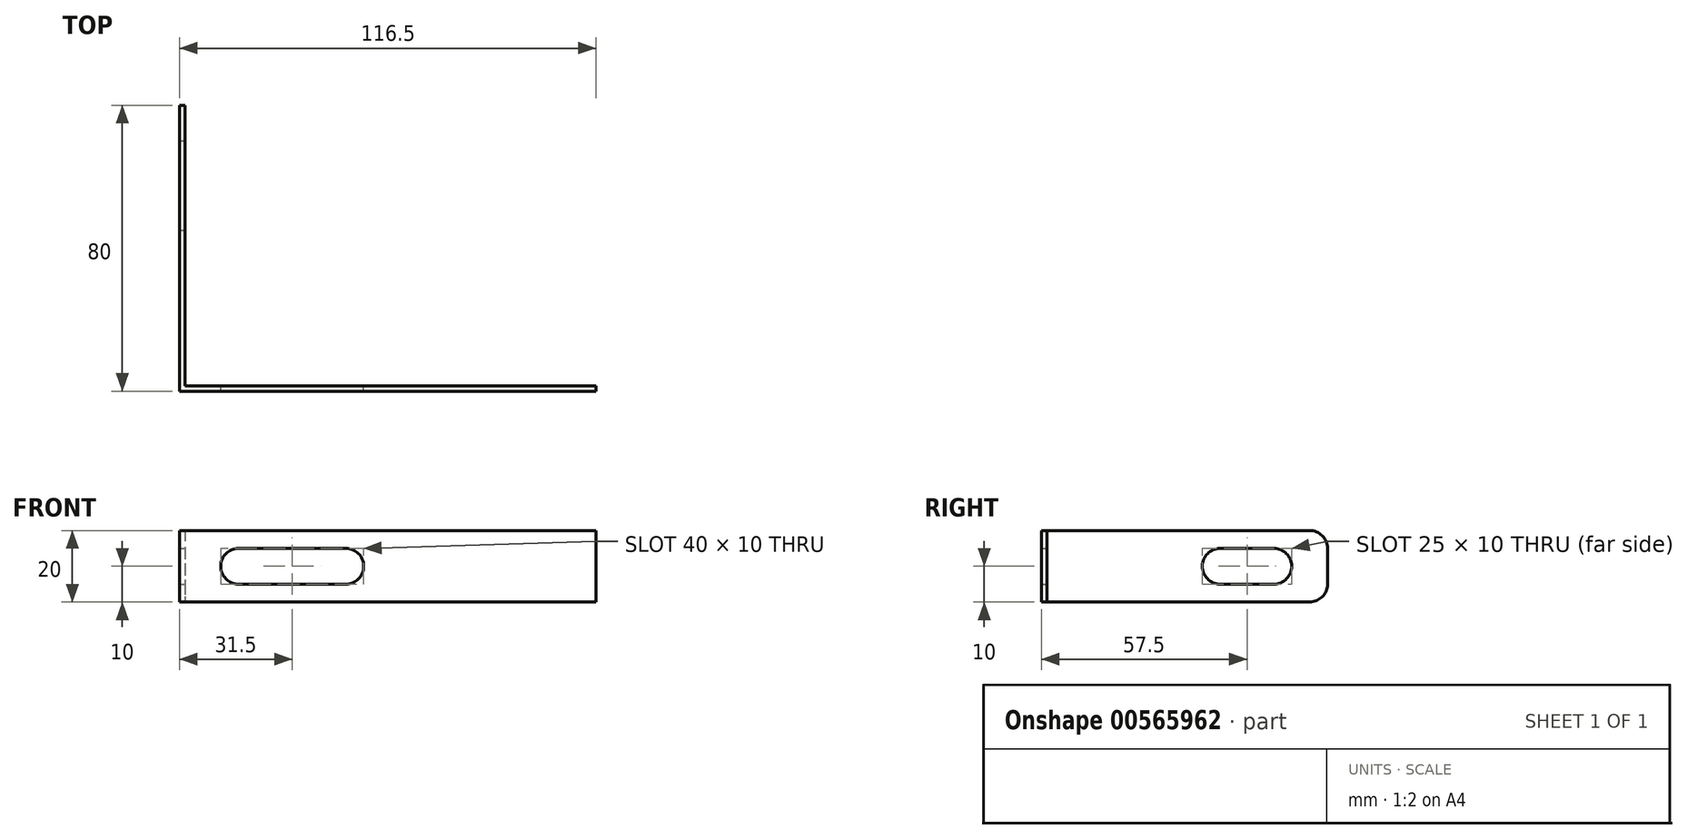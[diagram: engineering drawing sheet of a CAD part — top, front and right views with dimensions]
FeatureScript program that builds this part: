
annotation { "Feature Type Name" : "Feature", "Feature Type Description" : "" }
export const myFeature = defineFeature(function(context is Context, id is Id, definition is map)
    precondition{}
    {
        {
            var Q0;
            Q0=qCreatedBy(makeId("Front.planeOp"),FACE);
            var sketch = newSketch(context, id + "F0", { "sketchPlane" : qUnion([Q0])});
            skLineSegment(sketch, "E0", {"start": v(0, 10) * mm, "end": v(-115, 10) * mm});
            skLineSegment(sketch, "E1", {"start": v(-115, 10) * mm, "end": v(-115, -10) * mm});
            skLineSegment(sketch, "E2", {"start": v(-115, -10) * mm, "end": v(0, -10) * mm});
            skLineSegment(sketch, "E3.bottom", {"start": v(-70, -5) * mm, "end": v(-100, -5) * mm});
            skLineSegment(sketch, "E3.top", {"start": v(-70, 5) * mm, "end": v(-100, 5) * mm});
            skLineSegment(sketch, "E3.left", {"start": v(-65, 0) * mm, "end": v(-65, 0) * mm});
            skLineSegment(sketch, "E3.right", {"start": v(-105, 0) * mm, "end": v(-105, 0) * mm});
            skPoint(sketch, "E3.middle", {"position": v(-85, 0) * mm});
            skLineSegment(sketch, "E4.bottom", {"start": v(0, -5) * mm, "end": v(-50, -5) * mm});
            skLineSegment(sketch, "E4.top", {"start": v(0, 5) * mm, "end": v(-50, 5) * mm});
            skLineSegment(sketch, "E4.right", {"start": v(-55, 0) * mm, "end": v(-55, 0) * mm});
            skPoint(sketch, "E4.middle", {"position": v(-28.75, 0) * mm});
            skLineSegment(sketch, "E5", {"start": v(-60, 10) * mm, "end": v(-60, -10) * mm, "construction": true});
            skPoint(sketch, "E6.visualSharp", {"position": v(-105, 5) * mm});
            skArc(sketch, "E6.filletArc", {"start": v(-100, 5) * mm, "mid": v(-103.54, 3.54) * mm, "end": v(-105, 0) * mm});
            skPoint(sketch, "E7.visualSharp", {"position": v(-105, -5) * mm});
            skArc(sketch, "E7.filletArc", {"start": v(-105, 0) * mm, "mid": v(-103.54, -3.54) * mm, "end": v(-100, -5) * mm});
            skPoint(sketch, "E8.visualSharp", {"position": v(-65, -5) * mm});
            skArc(sketch, "E8.filletArc", {"start": v(-70, -5) * mm, "mid": v(-66.46, -3.54) * mm, "end": v(-65, 0) * mm});
            skPoint(sketch, "E9.visualSharp", {"position": v(-65, 5) * mm});
            skArc(sketch, "E9.filletArc", {"start": v(-65, 0) * mm, "mid": v(-66.46, 3.54) * mm, "end": v(-70, 5) * mm});
            skPoint(sketch, "E10.visualSharp", {"position": v(-55, 5) * mm});
            skArc(sketch, "E10.filletArc", {"start": v(-50, 5) * mm, "mid": v(-53.54, 3.54) * mm, "end": v(-55, 0) * mm});
            skPoint(sketch, "E11.visualSharp", {"position": v(-55, -5) * mm});
            skArc(sketch, "E11.filletArc", {"start": v(-55, 0) * mm, "mid": v(-53.54, -3.54) * mm, "end": v(-50, -5) * mm});
            skLineSegment(sketch, "E12", {"start": v(0, 10) * mm, "end": v(0, 0) * mm});
            skLineSegment(sketch, "E13", {"start": v(0, 0) * mm, "end": v(0, -10) * mm});
            skSolve(sketch);
        }
        {
            var Q0;
            Q0 = qSketchRegion(id + "F0", true);
            extrude(context, id + "F1", {"entities" : qUnion([Q0]), "depth" : 1.5 * mm, "offsetDistance" : 25 * mm});
        }
        {
            var Q0;
            Q0=makeQuery(id+"F1.opExtrude","SWEPT_FACE",FACE,{"disambiguationData":[OSD([sQuery(id+"F0.wireOp",EDGE,"E1")])]});
            var sketch = newSketch(context, id + "F2", { "sketchPlane" : qUnion([Q0])});
            skLineSegment(sketch, "E14.0", {"start": v(1.5, 10) * mm, "end": v(1.5, -10) * mm});
            skLineSegment(sketch, "E15", {"start": v(1.5, 10) * mm, "end": v(-73.5, 10) * mm});
            skLineSegment(sketch, "E16", {"start": v(-78.5, 5) * mm, "end": v(-78.5, -5) * mm});
            skLineSegment(sketch, "E17", {"start": v(-73.5, -10) * mm, "end": v(1.5, -10) * mm});
            skLineSegment(sketch, "E18", {"start": v(0, 0) * mm, "end": v(-78.5, 0) * mm, "construction": true});
            skPoint(sketch, "E18.endSnap0", {"position": v(-78.5, 0) * mm});
            skLineSegment(sketch, "E19.bottom", {"start": v(-63.5, -5) * mm, "end": v(-48.5, -5) * mm});
            skLineSegment(sketch, "E19.top", {"start": v(-63.5, 5) * mm, "end": v(-48.5, 5) * mm});
            skLineSegment(sketch, "E19.left", {"start": v(-68.5, 0) * mm, "end": v(-68.5, 0) * mm});
            skLineSegment(sketch, "E19.right", {"start": v(-43.5, 0) * mm, "end": v(-43.5, 0) * mm});
            skPoint(sketch, "E19.middle", {"position": v(-56, 0) * mm});
            skLineSegment(sketch, "E20", {"start": v(-34, 10) * mm, "end": v(-34, -10) * mm, "construction": true});
            skPoint(sketch, "E21.visualSharp", {"position": v(-68.5, 5) * mm});
            skArc(sketch, "E21.filletArc", {"start": v(-63.5, 5) * mm, "mid": v(-67.04, 3.54) * mm, "end": v(-68.5, 0) * mm});
            skPoint(sketch, "E22.visualSharp", {"position": v(-68.5, -5) * mm});
            skArc(sketch, "E22.filletArc", {"start": v(-68.5, 0) * mm, "mid": v(-67.04, -3.54) * mm, "end": v(-63.5, -5) * mm});
            skPoint(sketch, "E23.visualSharp", {"position": v(-43.5, -5) * mm});
            skArc(sketch, "E23.filletArc", {"start": v(-48.5, -5) * mm, "mid": v(-44.96, -3.54) * mm, "end": v(-43.5, 0) * mm});
            skPoint(sketch, "E24.visualSharp", {"position": v(-43.5, 5) * mm});
            skArc(sketch, "E24.filletArc", {"start": v(-43.5, 0) * mm, "mid": v(-44.96, 3.54) * mm, "end": v(-48.5, 5) * mm});
            skPoint(sketch, "E25.visualSharp", {"position": v(-78.5, 10) * mm});
            skArc(sketch, "E25.filletArc", {"start": v(-73.5, 10) * mm, "mid": v(-77.04, 8.54) * mm, "end": v(-78.5, 5) * mm});
            skPoint(sketch, "E26.visualSharp", {"position": v(-78.5, -10) * mm});
            skArc(sketch, "E26.filletArc", {"start": v(-78.5, -5) * mm, "mid": v(-77.04, -8.54) * mm, "end": v(-73.5, -10) * mm});
            skSolve(sketch);
        }
        {
            var Q0;
            Q0 = qSketchRegion(id + "F2", true);
            extrude(context, id + "F3", {"entities" : qUnion([Q0]), "operationType" : NewBodyOperationType.ADD, "depth" : 1.5 * mm, "offsetDistance" : 25 * mm});
        }
    });
